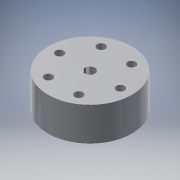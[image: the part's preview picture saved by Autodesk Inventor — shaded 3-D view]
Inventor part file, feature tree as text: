
AUTODESK INVENTOR PART (.ipt)
format: ipt  version: 2019.2 (Build 232265000, 265)  size: 569,344 bytes
history: native  units: mm
features: other x6, extrude x5, sketch x3, boolean_combine x1, plane x1, hole x1
ambient origin geometry x8: Origin, YZ Plane, XZ Plane, XY Plane, X Axis, Y Axis, Z Axis, Center Point
bodies: Solid1 (feature_tree), Solid3 (feature_tree)
feature tree (17):
  other  "MOT_WindowMotor_262100-3040.ipt"
  extrude  "Extrusion1"  Depth=30.0mm TaperAngle=0.0deg
  boolean_combine  "Combine2"
  other  "Thicken adapter hole"
  extrude  "Extrusion2"  Depth=0.225mm
  extrude  "Extrusion for middle hole"  Depth=4.5mm
  other  "Thicken Center Hole"
  extrude  "Extrusion for bolt holes"  Depth=2.0mm TaperAngle=0.0deg
  extrude  "Extrusion10"  Depth=4.5mm TaperAngle=0.0deg
  plane  "Work Plane1"
  sketch  "Sketch1"  dims[d0=70.0mm d1=30.0mm d2=0.0mm]
  other  "Solid1::MOT_WindowMotor_262100-3040.ipt"
  other  "TaggingFeature2"
  other  "Smooth Base"
  hole  "Hole to view fit"  [1 undecoded]
  sketch  "Sketch14"  dims[d7=10.0mm d8=0.225mm d9=0.5mm]
  sketch  "Sketch for bolt holes"  dims[d10=70.0mm d11=20.0mm d12=2.0mm d13=0.0mm d22=3.0mm d23=0.0mm d44=0.2mm d45=0.01mm d66=6.858mm d67=25.4mm d68=60.0mm d70=360.0deg d72=30.0mm d73=0.0mm d74=11.3665mm d75=60.0mm d77=360.0deg d79=4.5mm d80=0.0mm d81=35.0mm]
note: 1 required parameter value undecoded (feature->parameter linkage not recoverable at this tier; creation-order binding heuristic only, values carry confidence <= 0.55)
